# Revit family: Shower-Shower_Column_Kit-KOHLER-Urbanity-K-23749T_1
name_source: partatom
category: Plumbing Fixtures
units: mm (PartAtom-declared; Revit-internal decimal feet)

## family parameters
Cut with Voids When Loaded = No
Host = Face
OmniClass Number = 23.31.17.00
OmniClass Title = Showers
Part Type = Normal
Room Calculation Point = No
Round Connector Dimension = Use Diameter
Shared = No

## types (3) — shared parameters
ADA Compliant = No
Assembly Code = D2010700
CW Connection = Yes
Cold Water Inlet = Cold Water Inlet
Date Modified = 03/10/2023
Default Elevation = 42"
Description = Thermostat Three Outlet Shower Column – Manda overhead shower
Drain Included = No
Flow Rate = 0 GPM
HW Connection = Yes
Height = 47 15/16"
Hot Water Inlet = Hot Water Inlet
Length = 22 15/16"
Manufacturer = Kohler Co.
Master Format 2014 = 22 42 23
Master Format 2014 Name = Residential Showers
Material = Premium Metal Construction
Pressure = 0.00 psi
Product Documentation Link = https://files.kohler.com.cn
Product Name = Urbanity
Product Page URL = https://www.kohler.com.cn
Secondary Finish = Kohler-Plastic-GRC-Cool_Grey
URL = http://www.kohler.com.cn
Vent Connection = No
Waste Connection = No
Waste Water Outlet = Waste Water Outlet
WaterSense Certified = No
Width = 17 11/16"

## per-type parameters (varying)
| type | Finish | Model | Type |
| BL-Matte Black | Kohler-Metal-BL-Matte_Black | K-23749T-9-BL | 1 |
| CP-Polished Chrome | Kohler-Metal-CP-Polished_Chrome | K-23749T-9-CP | 2 |
| CY-Cloud Gray | Kohler-Metal-CY-Cloud_Gray | K-23749T-9-CY | 3 |

## geometry (parser evidence)
native form markers: Sweep x5
no freeform markers — native parametric forms only
